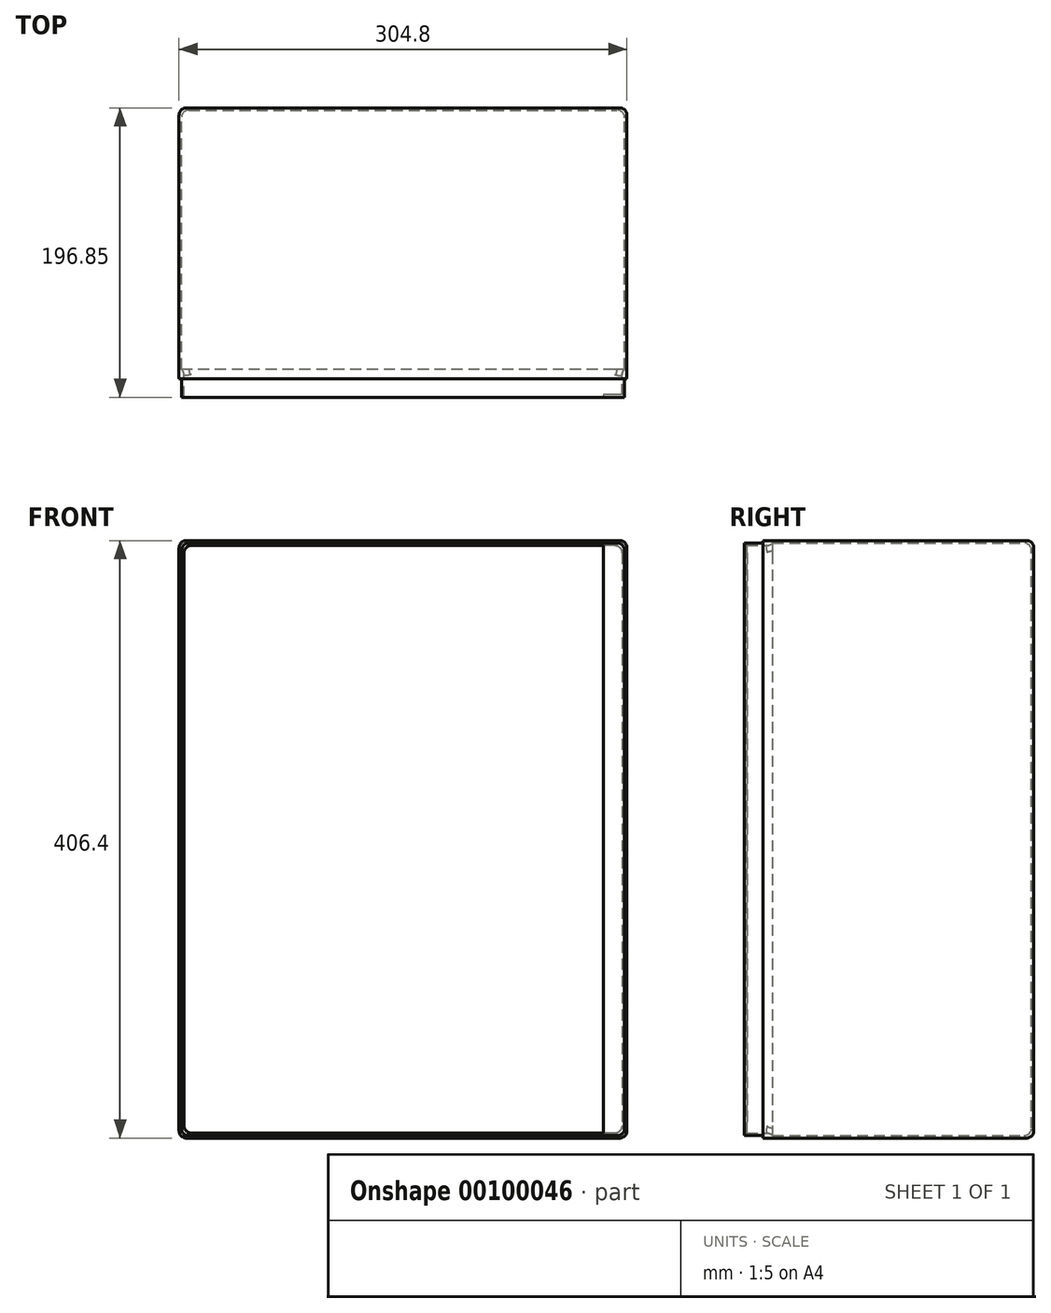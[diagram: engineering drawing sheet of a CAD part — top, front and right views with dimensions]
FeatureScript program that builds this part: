
annotation { "Feature Type Name" : "Feature", "Feature Type Description" : "" }
export const myFeature = defineFeature(function(context is Context, id is Id, definition is map)
    precondition{}
    {
        {
            var Q0;
            Q0=qCreatedBy(makeId("Front.planeOp"),FACE);
            var sketch = newSketch(context, id + "F0", { "sketchPlane" : qUnion([Q0])});
            skLineSegment(sketch, "E0.bottom", {"start": v(152.4, 203.2) * mm, "end": v(-152.4, 203.2) * mm});
            skLineSegment(sketch, "E0.top", {"start": v(152.4, -203.2) * mm, "end": v(-152.4, -203.2) * mm});
            skLineSegment(sketch, "E0.left", {"start": v(152.4, 203.2) * mm, "end": v(152.4, -203.2) * mm});
            skLineSegment(sketch, "E0.right", {"start": v(-152.4, 203.2) * mm, "end": v(-152.4, -203.2) * mm});
            skPoint(sketch, "E0.middle", {"position": v(0, 0) * mm});
            skSolve(sketch);
        }
        {
            var Q0;
            Q0 = qSketchRegion(id + "F0", true);
            extrude(context, id + "F1", {"entities" : qUnion([Q0]), "depth" : 1.65 * mm});
        }
        {
            var Q0;
            Q0=makeQuery(id+"F1.opExtrude","CAP_FACE",FACE,{"disambiguationData":[OSD([sQuery(id+"F0.wireOp",EDGE,"E0.bottom"),sQuery(id+"F0.wireOp",EDGE,"E0.top"),sQuery(id+"F0.wireOp",EDGE,"E0.left"),sQuery(id+"F0.wireOp",EDGE,"E0.right")])],"isStart":true});
            var sketch = newSketch(context, id + "F2", { "sketchPlane" : qUnion([Q0])});
            skLineSegment(sketch, "E1.0", {"start": v(-152.4, 203.2) * mm, "end": v(152.4, 203.2) * mm});
            skLineSegment(sketch, "E1.1", {"start": v(-152.4, 203.2) * mm, "end": v(-152.4, -203.2) * mm});
            skLineSegment(sketch, "E1.2", {"start": v(152.4, 203.2) * mm, "end": v(152.4, -203.2) * mm});
            skLineSegment(sketch, "E1.3", {"start": v(-152.4, -203.2) * mm, "end": v(152.4, -203.2) * mm});
            skLineSegment(sketch, "E2.0", {"start": v(-150.75, 201.55) * mm, "end": v(150.75, 201.55) * mm});
            skLineSegment(sketch, "E2.1", {"start": v(-150.75, 201.55) * mm, "end": v(-150.75, -201.55) * mm});
            skLineSegment(sketch, "E2.2", {"start": v(-150.75, -201.55) * mm, "end": v(150.75, -201.55) * mm});
            skLineSegment(sketch, "E2.3", {"start": v(150.75, 201.55) * mm, "end": v(150.75, -201.55) * mm});
            skSolve(sketch);
        }
        {
            var Q0;
            Q0 = qSketchRegion(id + "F2", true);
            extrude(context, id + "F3", {"entities" : qUnion([Q0]), "operationType" : NewBodyOperationType.ADD, "oppositeDirection" : true, "depth" : 184.15 * mm});
        }
        {
            var Q0;
            Q0=makeQuery(id+"F3.opExtrude","CAP_FACE",FACE,{"disambiguationData":[OSD([sQuery(id+"F2.wireOp",EDGE,"E1.0"),sQuery(id+"F2.wireOp",EDGE,"E1.1"),sQuery(id+"F2.wireOp",EDGE,"E1.2"),sQuery(id+"F2.wireOp",EDGE,"E1.3"),sQuery(id+"F2.wireOp",EDGE,"E2.0"),sQuery(id+"F2.wireOp",EDGE,"E2.1"),sQuery(id+"F2.wireOp",EDGE,"E2.2"),sQuery(id+"F2.wireOp",EDGE,"E2.3")])],"isStart":false});
            var sketch = newSketch(context, id + "F4", { "sketchPlane" : qUnion([Q0])});
            skLineSegment(sketch, "E3.0", {"start": v(149.1, 199.9) * mm, "end": v(-149.1, 199.9) * mm});
            skLineSegment(sketch, "E3.1", {"start": v(149.1, 199.9) * mm, "end": v(149.1, -199.9) * mm});
            skLineSegment(sketch, "E3.2", {"start": v(149.1, -199.9) * mm, "end": v(-149.1, -199.9) * mm});
            skLineSegment(sketch, "E3.3", {"start": v(-149.1, 199.9) * mm, "end": v(-149.1, -199.9) * mm});
            skLineSegment(sketch, "E4.0", {"start": v(150.75, 201.55) * mm, "end": v(-150.75, 201.55) * mm});
            skLineSegment(sketch, "E4.1", {"start": v(-150.75, 201.55) * mm, "end": v(-150.75, -201.55) * mm});
            skLineSegment(sketch, "E4.2", {"start": v(150.75, 201.55) * mm, "end": v(150.75, -201.55) * mm});
            skLineSegment(sketch, "E4.3", {"start": v(150.75, -201.55) * mm, "end": v(-150.75, -201.55) * mm});
            skSolve(sketch);
        }
        {
            var Q0;
            Q0 = qSketchRegion(id + "F4", true);
            extrude(context, id + "F5", {"entities" : qUnion([Q0]), "operationType" : NewBodyOperationType.ADD, "depth" : 12.7 * mm, "hasSecondDirection" : true, "secondDirectionOppositeDirection" : true, "secondDirectionDepth" : 6.35 * mm});
        }
        {
            var Q0;
            Q0=makeQuery(id+"F1.opExtrude","CAP_FACE",FACE,{"disambiguationData":[OSD([sQuery(id+"F0.wireOp",EDGE,"E0.bottom"),sQuery(id+"F0.wireOp",EDGE,"E0.top"),sQuery(id+"F0.wireOp",EDGE,"E0.left"),sQuery(id+"F0.wireOp",EDGE,"E0.right")])],"isStart":false});
            var Q1;
            Q1=makeQuery(id+"F3.opExtrude","SWEPT_EDGE",EDGE,{"disambiguationData":[OSD([sQuery(id+"F2.wireOp",EDGE,"E2.0"),sQuery(id+"F2.wireOp",EDGE,"E2.1")])]});
            var Q2;
            Q2=makeQuery(id+"F3.opExtrude","SWEPT_EDGE",EDGE,{"disambiguationData":[OSD([sQuery(id+"F2.wireOp",EDGE,"E2.0"),sQuery(id+"F2.wireOp",EDGE,"E2.3")])]});
            var Q3;
            Q3=makeQuery(id+"F3.opExtrude","SWEPT_EDGE",EDGE,{"disambiguationData":[OSD([sQuery(id+"F2.wireOp",EDGE,"E2.2"),sQuery(id+"F2.wireOp",EDGE,"E2.3")])]});
            var Q4;
            Q4=makeQuery(id+"F3.opExtrude","SWEPT_EDGE",EDGE,{"disambiguationData":[OSD([sQuery(id+"F2.wireOp",EDGE,"E2.1"),sQuery(id+"F2.wireOp",EDGE,"E2.2")])]});
            fillet(context, id + "F6", {"entities" : qUnion([Q0, Q1, Q2, Q3, Q4]), "radius" : 5.08 * mm, "tangentPropagation" : true, "allowEdgeOverflow" : false});
        }
        {
            var Q0;
            Q0=makeQuery(id+"F5.opExtrude","SWEPT_EDGE",EDGE,{"disambiguationData":[OSD([sQuery(id+"F4.wireOp",EDGE,"E3.0"),sQuery(id+"F4.wireOp",EDGE,"E3.3")])]});
            var Q1;
            Q1=makeQuery(id+"F5.opExtrude","SWEPT_EDGE",EDGE,{"disambiguationData":[OSD([sQuery(id+"F4.wireOp",EDGE,"E3.2"),sQuery(id+"F4.wireOp",EDGE,"E3.3")])]});
            var Q2;
            Q2=makeQuery(id+"F5.opExtrude","SWEPT_EDGE",EDGE,{"disambiguationData":[OSD([sQuery(id+"F4.wireOp",EDGE,"E3.1"),sQuery(id+"F4.wireOp",EDGE,"E3.2")])]});
            var Q3;
            Q3=makeQuery(id+"F5.opExtrude","SWEPT_EDGE",EDGE,{"disambiguationData":[OSD([sQuery(id+"F4.wireOp",EDGE,"E3.0"),sQuery(id+"F4.wireOp",EDGE,"E3.1")])]});
            fillet(context, id + "F7", {"entities" : qUnion([Q0, Q1, Q2, Q3]), "radius" : 5.08 * mm, "tangentPropagation" : true, "allowEdgeOverflow" : false});
        }
        {
            var Q0;
            Q0=makeQuery(id+"F5.opExtrude","CAP_EDGE",EDGE,{"disambiguationData":[OSD([sQuery(id+"F4.wireOp",EDGE,"E3.2")])],"isStart":true});
            fillet(context, id + "F8", {"entities" : qUnion([Q0]), "radius" : 5.08 * mm, "tangentPropagation" : true, "allowEdgeOverflow" : false});
        }
        {
            var Q0;
            Q0=makeQuery(id+"F1.opExtrude","CAP_EDGE",EDGE,{"disambiguationData":[OSD([sQuery(id+"F0.wireOp",EDGE,"E0.left")])],"isStart":true});
            var Q1;
            Q1=makeQuery(id+"F1.opExtrude","CAP_EDGE",EDGE,{"disambiguationData":[OSD([sQuery(id+"F0.wireOp",EDGE,"E0.bottom")])],"isStart":true});
            var Q2;
            Q2=makeQuery(id+"F3.boolean.opBoolean","MERGE",EDGE,{"derivedFrom":[makeQuery(id+"F1.opExtrude","SWEPT_EDGE",EDGE,{"disambiguationData":[OSD([sQuery(id+"F0.wireOp",EDGE,"E0.bottom"),sQuery(id+"F0.wireOp",EDGE,"E0.left")])]}),makeQuery(id+"F3.opExtrude","SWEPT_EDGE",EDGE,{"disambiguationData":[OSD([sQuery(id+"F2.wireOp",EDGE,"E1.0"),sQuery(id+"F2.wireOp",EDGE,"E1.1")])]})]});
            var Q3;
            Q3=makeQuery(id+"F3.boolean.opBoolean","MERGE",EDGE,{"derivedFrom":[makeQuery(id+"F1.opExtrude","SWEPT_EDGE",EDGE,{"disambiguationData":[OSD([sQuery(id+"F0.wireOp",EDGE,"E0.bottom"),sQuery(id+"F0.wireOp",EDGE,"E0.right")])]}),makeQuery(id+"F3.opExtrude","SWEPT_EDGE",EDGE,{"disambiguationData":[OSD([sQuery(id+"F2.wireOp",EDGE,"E1.0"),sQuery(id+"F2.wireOp",EDGE,"E1.2")])]})]});
            var Q4;
            Q4=makeQuery(id+"F1.opExtrude","CAP_EDGE",EDGE,{"disambiguationData":[OSD([sQuery(id+"F0.wireOp",EDGE,"E0.right")])],"isStart":true});
            var Q5;
            Q5=makeQuery(id+"F3.boolean.opBoolean","MERGE",EDGE,{"derivedFrom":[makeQuery(id+"F1.opExtrude","SWEPT_EDGE",EDGE,{"disambiguationData":[OSD([sQuery(id+"F0.wireOp",EDGE,"E0.top"),sQuery(id+"F0.wireOp",EDGE,"E0.right")])]}),makeQuery(id+"F3.opExtrude","SWEPT_EDGE",EDGE,{"disambiguationData":[OSD([sQuery(id+"F2.wireOp",EDGE,"E1.2"),sQuery(id+"F2.wireOp",EDGE,"E1.3")])]})]});
            var Q6;
            Q6=makeQuery(id+"F1.opExtrude","CAP_EDGE",EDGE,{"disambiguationData":[OSD([sQuery(id+"F0.wireOp",EDGE,"E0.top")])],"isStart":true});
            var Q7;
            Q7=makeQuery(id+"F3.boolean.opBoolean","MERGE",EDGE,{"derivedFrom":[makeQuery(id+"F1.opExtrude","SWEPT_EDGE",EDGE,{"disambiguationData":[OSD([sQuery(id+"F0.wireOp",EDGE,"E0.top"),sQuery(id+"F0.wireOp",EDGE,"E0.left")])]}),makeQuery(id+"F3.opExtrude","SWEPT_EDGE",EDGE,{"disambiguationData":[OSD([sQuery(id+"F2.wireOp",EDGE,"E1.1"),sQuery(id+"F2.wireOp",EDGE,"E1.3")])]})]});
            fillet(context, id + "F9", {"entities" : qUnion([Q0, Q1, Q2, Q3, Q4, Q5, Q6, Q7]), "radius" : 5.08 * mm, "tangentPropagation" : true, "allowEdgeOverflow" : false});
        }
        {
            var Q0;
            Q0=makeQuery(id+"F5.opExtrude","SWEPT_EDGE",EDGE,{"disambiguationData":[OSD([sQuery(id+"F4.wireOp",EDGE,"E4.2"),sQuery(id+"F4.wireOp",EDGE,"E4.3")])]});
            var Q1;
            Q1=makeQuery(id+"F5.opExtrude","SWEPT_EDGE",EDGE,{"disambiguationData":[OSD([sQuery(id+"F4.wireOp",EDGE,"E4.1"),sQuery(id+"F4.wireOp",EDGE,"E4.3")])]});
            var Q2;
            Q2=makeQuery(id+"F5.opExtrude","SWEPT_EDGE",EDGE,{"disambiguationData":[OSD([sQuery(id+"F4.wireOp",EDGE,"E4.0"),sQuery(id+"F4.wireOp",EDGE,"E4.1")])]});
            var Q3;
            Q3=makeQuery(id+"F5.opExtrude","SWEPT_EDGE",EDGE,{"disambiguationData":[OSD([sQuery(id+"F4.wireOp",EDGE,"E4.0"),sQuery(id+"F4.wireOp",EDGE,"E4.2")])]});
            fillet(context, id + "F10", {"entities" : qUnion([Q0, Q1, Q2, Q3]), "radius" : 5.08 * mm, "tangentPropagation" : true, "allowEdgeOverflow" : false});
        }
        {
            var Q0;
            Q0=makeQuery(id+"F5.opExtrude","CAP_FACE",FACE,{"disambiguationData":[OSD([sQuery(id+"F4.wireOp",EDGE,"E3.0"),sQuery(id+"F4.wireOp",EDGE,"E3.1"),sQuery(id+"F4.wireOp",EDGE,"E3.2"),sQuery(id+"F4.wireOp",EDGE,"E3.3"),sQuery(id+"F4.wireOp",EDGE,"E4.0"),sQuery(id+"F4.wireOp",EDGE,"E4.1"),sQuery(id+"F4.wireOp",EDGE,"E4.2"),sQuery(id+"F4.wireOp",EDGE,"E4.3")])],"isStart":false});
            var sketch = newSketch(context, id + "F11", { "sketchPlane" : qUnion([Q0])});
            skLineSegment(sketch, "E5.0", {"start": v(144.02, 199.9) * mm, "end": v(136.4, 199.9) * mm});
            skArc(sketch, "E5.1", {"start": v(144.02, 199.9) * mm, "mid": v(147.61, 198.41) * mm, "end": v(149.1, 194.82) * mm});
            skLineSegment(sketch, "E5.2", {"start": v(149.1, 194.82) * mm, "end": v(149.1, -194.82) * mm});
            skArc(sketch, "E5.3", {"start": v(149.1, -194.82) * mm, "mid": v(147.61, -198.41) * mm, "end": v(144.02, -199.9) * mm});
            skLineSegment(sketch, "E5.4", {"start": v(144.02, -199.9) * mm, "end": v(136.4, -199.9) * mm});
            skLineSegment(sketch, "E6", {"start": v(136.4, -199.9) * mm, "end": v(136.4, 199.9) * mm});
            skSolve(sketch);
        }
        {
            var Q0;
            Q0 = qSketchRegion(id + "F11", true);
            extrude(context, id + "F12", {"entities" : qUnion([Q0]), "operationType" : NewBodyOperationType.ADD, "oppositeDirection" : true, "depth" : 1.65 * mm});
        }
    });
